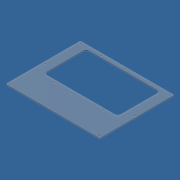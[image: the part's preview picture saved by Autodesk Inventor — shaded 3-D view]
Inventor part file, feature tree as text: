
AUTODESK INVENTOR PART (.ipt)
format: ipt  version: 2015 SP2 (Build 190223200, 223)  size: 150,016 bytes
history: native  units: mm (DEFAULTED — no unit token found)
features: other x8, sketch x2, hole x2, extrude x1, fillet x1
bodies: Solide1 (feature_tree)
feature tree (14):
  other  "Origine"
  sketch  "Esquisse1"
  extrude  "Extrusion1"  Depth=193.0mm
  hole  "Perçage6"  [1 undecoded]
  fillet  "Congé1"  Radius=8.0mm
  hole  "Perçage4"  [1 undecoded]
  other  "Plan YZ"
  other  "Plan XZ"
  other  "Plan XY"
  other  "Axe X"
  other  "Axe Y"
  other  "Axe Z"
  other  "Point de centre"
  sketch  "Esquisse9"
note: 2 required parameter values undecoded (feature->parameter linkage not recoverable at this tier; creation-order binding heuristic only, values carry confidence <= 0.55)
